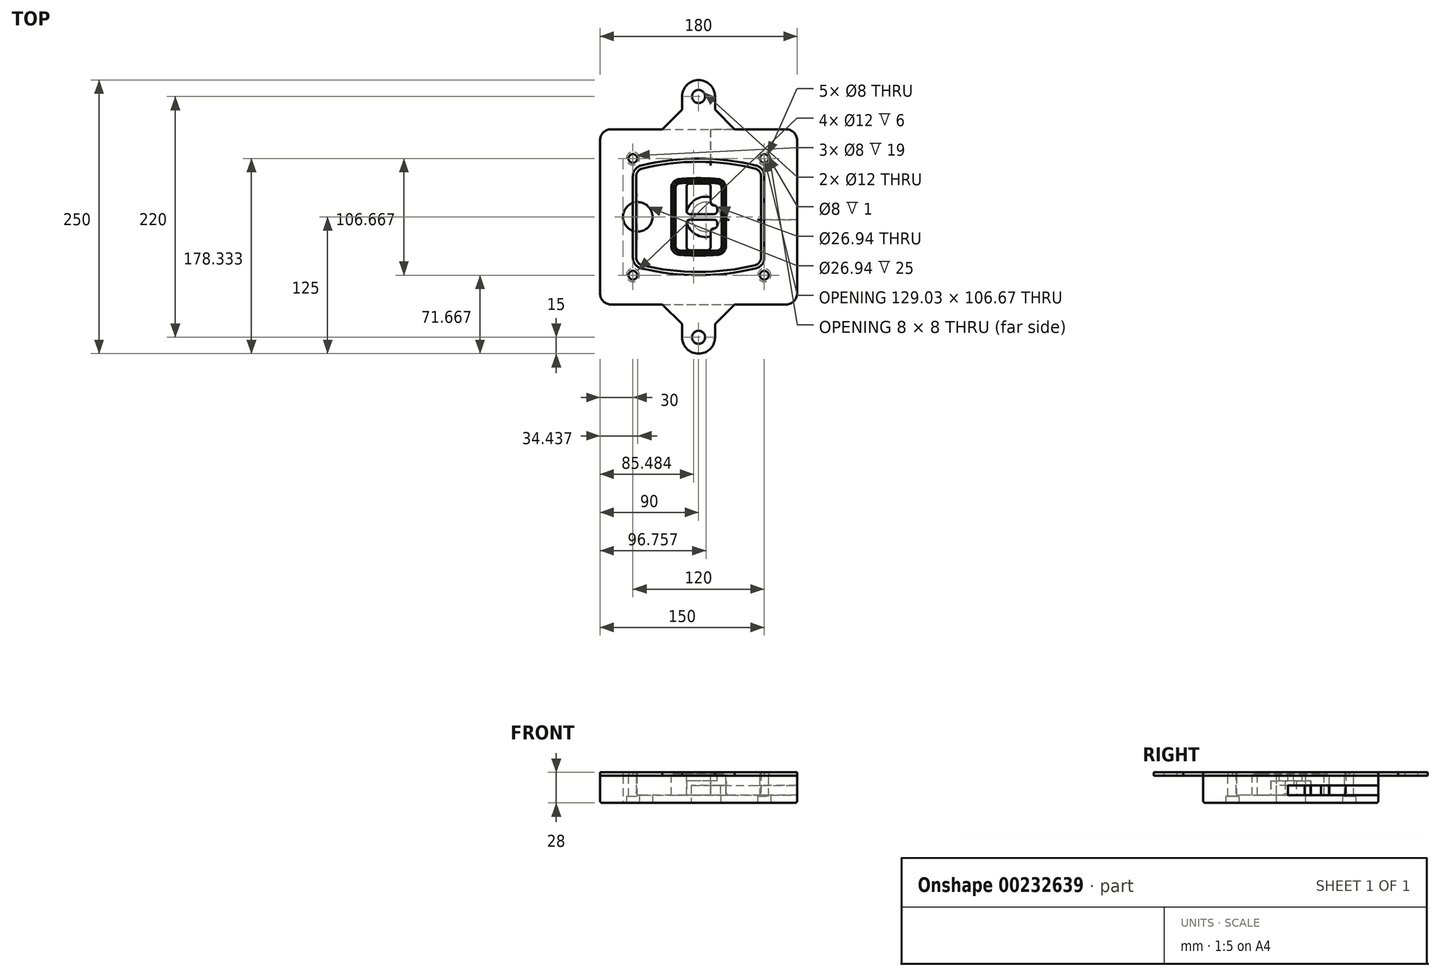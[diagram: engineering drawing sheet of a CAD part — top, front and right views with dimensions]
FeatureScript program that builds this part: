
annotation { "Feature Type Name" : "Feature", "Feature Type Description" : "" }
export const myFeature = defineFeature(function(context is Context, id is Id, definition is map)
    precondition{}
    {
        {
            var Q0;
            Q0=qCreatedBy(makeId("Top.planeOp"),FACE);
            var sketch = newSketch(context, id + "F0", { "sketchPlane" : qUnion([Q0])});
            skPoint(sketch, "E0.rect.middle", {"position": v(0, 0) * mm});
            skLineSegment(sketch, "E1.bottom", {"start": v(-80, -80) * mm, "end": v(80, -80) * mm});
            skLineSegment(sketch, "E1.top", {"start": v(-80, 80) * mm, "end": v(80, 80) * mm});
            skLineSegment(sketch, "E1.left", {"start": v(-90, -70) * mm, "end": v(-90, 70) * mm});
            skLineSegment(sketch, "E1.right", {"start": v(90, -70) * mm, "end": v(90, 70) * mm});
            skLineSegment(sketch, "E2", {"start": v(-90, 80) * mm, "end": v(90, -80) * mm, "construction": true});
            skLineSegment(sketch, "E3", {"start": v(90, 80) * mm, "end": v(-90, -80) * mm, "construction": true});
            skCircle(sketch, "E4", {"center": v(-60, 53.33) * mm, "radius": 4 * mm});
            skCircle(sketch, "E5", {"center": v(60, 53.33) * mm, "radius": 4 * mm});
            skCircle(sketch, "E6", {"center": v(60, -53.33) * mm, "radius": 4 * mm});
            skCircle(sketch, "E7", {"center": v(-60, -53.33) * mm, "radius": 4 * mm});
            skLineSegment(sketch, "E8", {"start": v(-60, 53.33) * mm, "end": v(60, 53.33) * mm, "construction": true});
            skLineSegment(sketch, "E9", {"start": v(60, 53.33) * mm, "end": v(60, -53.33) * mm, "construction": true});
            skLineSegment(sketch, "E10", {"start": v(60, -53.33) * mm, "end": v(-60, -53.33) * mm, "construction": true});
            skLineSegment(sketch, "E11", {"start": v(-60, -53.33) * mm, "end": v(-60, 53.33) * mm, "construction": true});
            skLineSegment(sketch, "E12", {"start": v(-60, 37.3) * mm, "end": v(-60, -37.3) * mm});
            skLineSegment(sketch, "E13", {"start": v(60, 37.3) * mm, "end": v(60, -37.3) * mm});
            skArc(sketch, "E14", {"start": v(52.38, 47.01) * mm, "mid": v(0, 53.33) * mm, "end": v(-52.38, 47.01) * mm});
            skArc(sketch, "E15", {"start": v(-52.38, -47.01) * mm, "mid": v(0, -53.33) * mm, "end": v(52.38, -47.01) * mm});
            skLineSegment(sketch, "E16", {"start": v(-60, 0) * mm, "end": v(60, 0) * mm, "construction": true});
            skPoint(sketch, "E17.visualSharp", {"position": v(-60, -45) * mm});
            skArc(sketch, "E17.filletArc", {"start": v(-60, -37.3) * mm, "mid": v(-57.87, -43.47) * mm, "end": v(-52.38, -47.01) * mm});
            skPoint(sketch, "E18.visualSharp", {"position": v(-60, 45) * mm});
            skArc(sketch, "E18.filletArc", {"start": v(-52.38, 47.01) * mm, "mid": v(-57.87, 43.47) * mm, "end": v(-60, 37.3) * mm});
            skPoint(sketch, "E19.visualSharp", {"position": v(60, 45) * mm});
            skArc(sketch, "E19.filletArc", {"start": v(60, 37.3) * mm, "mid": v(57.87, 43.47) * mm, "end": v(52.38, 47.01) * mm});
            skPoint(sketch, "E20.visualSharp", {"position": v(60, -45) * mm});
            skArc(sketch, "E20.filletArc", {"start": v(52.38, -47.01) * mm, "mid": v(57.87, -43.47) * mm, "end": v(60, -37.3) * mm});
            skPoint(sketch, "E21.visualSharp", {"position": v(-90, 80) * mm});
            skArc(sketch, "E21.filletArc", {"start": v(-80, 80) * mm, "mid": v(-87.07, 77.07) * mm, "end": v(-90, 70) * mm});
            skPoint(sketch, "E22.visualSharp", {"position": v(90, 80) * mm});
            skArc(sketch, "E22.filletArc", {"start": v(90, 70) * mm, "mid": v(87.07, 77.07) * mm, "end": v(80, 80) * mm});
            skPoint(sketch, "E23.visualSharp", {"position": v(90, -80) * mm});
            skArc(sketch, "E23.filletArc", {"start": v(80, -80) * mm, "mid": v(87.07, -77.07) * mm, "end": v(90, -70) * mm});
            skPoint(sketch, "E24.visualSharp", {"position": v(-90, -80) * mm});
            skArc(sketch, "E24.filletArc", {"start": v(-90, -70) * mm, "mid": v(-87.07, -77.07) * mm, "end": v(-80, -80) * mm});
            skArc(sketch, "E25.0", {"start": v(57, 37.3) * mm, "mid": v(55.5, 41.62) * mm, "end": v(51.67, 44.1) * mm});
            skLineSegment(sketch, "E25.1", {"start": v(57, 37.3) * mm, "end": v(57, -37.3) * mm});
            skArc(sketch, "E25.2", {"start": v(51.67, -44.1) * mm, "mid": v(55.5, -41.62) * mm, "end": v(57, -37.3) * mm});
            skArc(sketch, "E25.3", {"start": v(-51.67, -44.1) * mm, "mid": v(0, -50.33) * mm, "end": v(51.67, -44.1) * mm});
            skArc(sketch, "E25.4", {"start": v(-57, -37.3) * mm, "mid": v(-55.5, -41.62) * mm, "end": v(-51.67, -44.1) * mm});
            skArc(sketch, "E25.5", {"start": v(51.67, 44.1) * mm, "mid": v(0, 50.33) * mm, "end": v(-51.67, 44.1) * mm});
            skLineSegment(sketch, "E25.6", {"start": v(-57, 37.3) * mm, "end": v(-57, -37.3) * mm});
            skArc(sketch, "E25.7", {"start": v(-51.67, 44.1) * mm, "mid": v(-55.5, 41.62) * mm, "end": v(-57, 37.3) * mm});
            skArc(sketch, "E26.0", {"start": v(-53.33, 50.9) * mm, "mid": v(-61.01, 45.94) * mm, "end": v(-64, 37.3) * mm});
            skArc(sketch, "E26.1", {"start": v(53.33, 50.9) * mm, "mid": v(0, 57.33) * mm, "end": v(-53.33, 50.9) * mm});
            skArc(sketch, "E26.2", {"start": v(64, 37.3) * mm, "mid": v(61.01, 45.94) * mm, "end": v(53.33, 50.9) * mm});
            skLineSegment(sketch, "E26.3", {"start": v(64, 37.3) * mm, "end": v(64, -37.3) * mm});
            skArc(sketch, "E26.4", {"start": v(53.33, -50.9) * mm, "mid": v(61.01, -45.94) * mm, "end": v(64, -37.3) * mm});
            skLineSegment(sketch, "E26.5", {"start": v(-64, 37.3) * mm, "end": v(-64, -37.3) * mm});
            skArc(sketch, "E26.6", {"start": v(-53.33, -50.9) * mm, "mid": v(0, -57.33) * mm, "end": v(53.33, -50.9) * mm});
            skArc(sketch, "E26.7", {"start": v(-64, -37.3) * mm, "mid": v(-61.01, -45.94) * mm, "end": v(-53.33, -50.9) * mm});
            skSolve(sketch);
        }
        {
            var Q0;
            Q0=makeQuery(id+"F0.imprint","IMPRINT",FACE,{"disambiguationData":[TD([[makeQuery(id+"F0.imprint","IMPRINT",EDGE,{"derivedFrom":sQuery(id+"F0.wireOp",EDGE,"E1.bottom")}),1.0]])]});
            var Q1;
            Q1=makeQuery(id+"F0.imprint","IMPRINT",FACE,{"disambiguationData":[TD([[makeQuery(id+"F0.imprint","IMPRINT",EDGE,{"derivedFrom":sQuery(id+"F0.wireOp",EDGE,"E12")}),1.0]])]});
            var Q2;
            Q2=makeQuery(id+"F0.imprint","IMPRINT",FACE,{"disambiguationData":[TD([[makeQuery(id+"F0.imprint","IMPRINT",EDGE,{"derivedFrom":sQuery(id+"F0.wireOp",EDGE,"E25.0")}),1.0]])]});
            var Q3;
            Q3=makeQuery(id+"F0.imprint","IMPRINT",FACE,{"disambiguationData":[TD([[makeQuery(id+"F0.imprint","IMPRINT",EDGE,{"derivedFrom":sQuery(id+"F0.wireOp",EDGE,"E12")}),-1.0]])]});
            extrude(context, id + "F1", {"entities" : qUnion([Q0, Q1, Q2, Q3]), "oppositeDirection" : true, "depth" : 25 * mm});
        }
        {
            var Q0;
            Q0=makeQuery(id+"F0.imprint","IMPRINT",FACE,{"disambiguationData":[TD([[makeQuery(id+"F0.imprint","IMPRINT",EDGE,{"derivedFrom":sQuery(id+"F0.wireOp",EDGE,"E12")}),1.0]])]});
            extrude(context, id + "F2", {"entities" : qUnion([Q0]), "operationType" : NewBodyOperationType.ADD, "depth" : 3 * mm});
        }
        {
            var Q0;
            Q0=makeQuery(id+"F0.imprint","IMPRINT",FACE,{"disambiguationData":[TD([[makeQuery(id+"F0.imprint","IMPRINT",EDGE,{"derivedFrom":sQuery(id+"F0.wireOp",EDGE,"E25.0")}),1.0]])]});
            extrude(context, id + "F3", {"entities" : qUnion([Q0]), "operationType" : NewBodyOperationType.REMOVE, "oppositeDirection" : true, "depth" : 18 * mm});
        }
        {
            var Q0;
            Q0=makeQuery(id+"F2.opExtrude","CAP_FACE",FACE,{"disambiguationData":[OSD([sQuery(id+"F0.wireOp",EDGE,"E12"),sQuery(id+"F0.wireOp",EDGE,"E13"),sQuery(id+"F0.wireOp",EDGE,"E14"),sQuery(id+"F0.wireOp",EDGE,"E15"),sQuery(id+"F0.wireOp",EDGE,"E17.filletArc"),sQuery(id+"F0.wireOp",EDGE,"E18.filletArc"),sQuery(id+"F0.wireOp",EDGE,"E19.filletArc"),sQuery(id+"F0.wireOp",EDGE,"E20.filletArc"),sQuery(id+"F0.wireOp",EDGE,"E25.0"),sQuery(id+"F0.wireOp",EDGE,"E25.1"),sQuery(id+"F0.wireOp",EDGE,"E25.2"),sQuery(id+"F0.wireOp",EDGE,"E25.3"),sQuery(id+"F0.wireOp",EDGE,"E25.4"),sQuery(id+"F0.wireOp",EDGE,"E25.5"),sQuery(id+"F0.wireOp",EDGE,"E25.6"),sQuery(id+"F0.wireOp",EDGE,"E25.7")])],"isStart":false});
            var sketch = newSketch(context, id + "F4", { "sketchPlane" : qUnion([Q0])});
            skArc(sketch, "E27.0", {"start": v(-17.7, -34.56) * mm, "mid": v(0, -35.33) * mm, "end": v(17.7, -34.56) * mm});
            skArc(sketch, "E28.0", {"start": v(17.7, 34.56) * mm, "mid": v(0, 35.33) * mm, "end": v(-17.7, 34.56) * mm});
            skLineSegment(sketch, "E29", {"start": v(-25, 26.59) * mm, "end": v(-25, -26.59) * mm});
            skLineSegment(sketch, "E30", {"start": v(25, 26.59) * mm, "end": v(25, -26.59) * mm});
            skLineSegment(sketch, "E31", {"start": v(-25, 33.78) * mm, "end": v(25, 33.78) * mm, "construction": true});
            skLineSegment(sketch, "E32", {"start": v(-25, -33.78) * mm, "end": v(25, -33.78) * mm, "construction": true});
            skPoint(sketch, "E33.visualSharp", {"position": v(-25, 33.78) * mm});
            skArc(sketch, "E33.filletArc", {"start": v(-17.7, 34.56) * mm, "mid": v(-22.9, 32) * mm, "end": v(-25, 26.59) * mm});
            skPoint(sketch, "E34.visualSharp", {"position": v(25, 33.78) * mm});
            skArc(sketch, "E34.filletArc", {"start": v(25, 26.59) * mm, "mid": v(22.9, 32) * mm, "end": v(17.7, 34.56) * mm});
            skPoint(sketch, "E35.visualSharp", {"position": v(25, -33.78) * mm});
            skArc(sketch, "E35.filletArc", {"start": v(17.7, -34.56) * mm, "mid": v(22.9, -32) * mm, "end": v(25, -26.59) * mm});
            skPoint(sketch, "E36.visualSharp", {"position": v(-25, -33.78) * mm});
            skArc(sketch, "E36.filletArc", {"start": v(-25, -26.59) * mm, "mid": v(-22.9, -32) * mm, "end": v(-17.7, -34.56) * mm});
            skArc(sketch, "E37.0", {"start": v(51.67, 44.1) * mm, "mid": v(0, 50.33) * mm, "end": v(-51.67, 44.1) * mm});
            skArc(sketch, "E37.1", {"start": v(-51.67, 44.1) * mm, "mid": v(-55.5, 41.62) * mm, "end": v(-57, 37.3) * mm});
            skLineSegment(sketch, "E37.2", {"start": v(-57, 37.3) * mm, "end": v(-57, -37.3) * mm});
            skArc(sketch, "E37.3", {"start": v(-57, -37.3) * mm, "mid": v(-55.5, -41.62) * mm, "end": v(-51.67, -44.1) * mm});
            skArc(sketch, "E37.4", {"start": v(-51.67, -44.1) * mm, "mid": v(0, -50.33) * mm, "end": v(51.67, -44.1) * mm});
            skArc(sketch, "E37.5", {"start": v(51.67, -44.1) * mm, "mid": v(55.5, -41.62) * mm, "end": v(57, -37.3) * mm});
            skLineSegment(sketch, "E37.6", {"start": v(57, 37.3) * mm, "end": v(57, -37.3) * mm});
            skArc(sketch, "E37.7", {"start": v(57, 37.3) * mm, "mid": v(55.5, 41.62) * mm, "end": v(51.67, 44.1) * mm});
            skLineSegment(sketch, "E38.0", {"start": v(23, 26.59) * mm, "end": v(23, -26.59) * mm});
            skArc(sketch, "E38.1", {"start": v(17.53, -32.56) * mm, "mid": v(21.42, -30.64) * mm, "end": v(23, -26.59) * mm});
            skArc(sketch, "E38.2", {"start": v(-17.53, -32.56) * mm, "mid": v(0, -33.33) * mm, "end": v(17.53, -32.56) * mm});
            skArc(sketch, "E38.3", {"start": v(-23, -26.59) * mm, "mid": v(-21.42, -30.64) * mm, "end": v(-17.53, -32.56) * mm});
            skLineSegment(sketch, "E38.4", {"start": v(-23, 26.59) * mm, "end": v(-23, -26.59) * mm});
            skArc(sketch, "E38.5", {"start": v(23, 26.59) * mm, "mid": v(21.42, 30.64) * mm, "end": v(17.53, 32.56) * mm});
            skArc(sketch, "E38.6", {"start": v(-17.53, 32.56) * mm, "mid": v(-21.42, 30.64) * mm, "end": v(-23, 26.59) * mm});
            skArc(sketch, "E38.7", {"start": v(17.53, 32.56) * mm, "mid": v(0, 33.33) * mm, "end": v(-17.53, 32.56) * mm});
            skArc(sketch, "E39.0", {"start": v(21, 26.59) * mm, "mid": v(19.95, 29.29) * mm, "end": v(17.35, 30.57) * mm});
            skLineSegment(sketch, "E39.1", {"start": v(21, 26.59) * mm, "end": v(21, -26.59) * mm});
            skArc(sketch, "E39.2", {"start": v(17.35, -30.57) * mm, "mid": v(19.95, -29.29) * mm, "end": v(21, -26.59) * mm});
            skArc(sketch, "E39.3", {"start": v(-17.35, -30.57) * mm, "mid": v(0, -31.33) * mm, "end": v(17.35, -30.57) * mm});
            skArc(sketch, "E39.4", {"start": v(-21, -26.59) * mm, "mid": v(-19.95, -29.29) * mm, "end": v(-17.35, -30.57) * mm});
            skArc(sketch, "E39.5", {"start": v(17.35, 30.57) * mm, "mid": v(0, 31.33) * mm, "end": v(-17.35, 30.57) * mm});
            skLineSegment(sketch, "E39.6", {"start": v(-21, 26.59) * mm, "end": v(-21, -26.59) * mm});
            skArc(sketch, "E39.7", {"start": v(-17.35, 30.57) * mm, "mid": v(-19.95, 29.29) * mm, "end": v(-21, 26.59) * mm});
            skLineSegment(sketch, "E40", {"start": v(-25, 0) * mm, "end": v(25, 0) * mm, "construction": true});
            skLineSegment(sketch, "E41", {"start": v(-11, 5.5) * mm, "end": v(-11, 27.5) * mm});
            skLineSegment(sketch, "E42", {"start": v(-8, 30.5) * mm, "end": v(8, 30.5) * mm});
            skLineSegment(sketch, "E43", {"start": v(11, 27.5) * mm, "end": v(11, 13.5) * mm});
            skLineSegment(sketch, "E44", {"start": v(14, 10.5) * mm, "end": v(14, 10.5) * mm});
            skLineSegment(sketch, "E45", {"start": v(17, 7.5) * mm, "end": v(17, 5.5) * mm});
            skLineSegment(sketch, "E46", {"start": v(14, 2.5) * mm, "end": v(-8, 2.5) * mm});
            skPoint(sketch, "E47.visualSharp", {"position": v(-11, 30.5) * mm});
            skArc(sketch, "E47.filletArc", {"start": v(-8, 30.5) * mm, "mid": v(-10.12, 29.62) * mm, "end": v(-11, 27.5) * mm});
            skPoint(sketch, "E48.visualSharp", {"position": v(11, 30.5) * mm});
            skArc(sketch, "E48.filletArc", {"start": v(11, 27.5) * mm, "mid": v(10.12, 29.62) * mm, "end": v(8, 30.5) * mm});
            skPoint(sketch, "E49.visualSharp", {"position": v(11, 10.5) * mm});
            skArc(sketch, "E49.filletArc", {"start": v(11, 13.5) * mm, "mid": v(11.88, 11.38) * mm, "end": v(14, 10.5) * mm});
            skPoint(sketch, "E50.visualSharp", {"position": v(17, 10.5) * mm});
            skArc(sketch, "E50.filletArc", {"start": v(17, 7.5) * mm, "mid": v(16.12, 9.62) * mm, "end": v(14, 10.5) * mm});
            skPoint(sketch, "E51.visualSharp", {"position": v(17, 2.5) * mm});
            skArc(sketch, "E51.filletArc", {"start": v(14, 2.5) * mm, "mid": v(16.12, 3.38) * mm, "end": v(17, 5.5) * mm});
            skPoint(sketch, "E52.visualSharp", {"position": v(-11, 2.5) * mm});
            skArc(sketch, "E52.filletArc", {"start": v(-11, 5.5) * mm, "mid": v(-10.12, 3.38) * mm, "end": v(-8, 2.5) * mm});
            skLineSegment(sketch, "E53.0.MirrorCS", {"start": v(14, -2.5) * mm, "end": v(-8, -2.5) * mm});
            skArc(sketch, "E54.0.MirrorCS", {"start": v(-11, -5.5) * mm, "mid": v(-10.12, -3.38) * mm, "end": v(-8, -2.5) * mm});
            skLineSegment(sketch, "E55.0.MirrorCS", {"start": v(-11, -5.5) * mm, "end": v(-11, -27.5) * mm});
            skArc(sketch, "E56.0.MirrorCS", {"start": v(-8, -30.5) * mm, "mid": v(-10.12, -29.62) * mm, "end": v(-11, -27.5) * mm});
            skLineSegment(sketch, "E57.0.MirrorCS", {"start": v(-8, -30.5) * mm, "end": v(8, -30.5) * mm});
            skArc(sketch, "E58.0.MirrorCS", {"start": v(11, -27.5) * mm, "mid": v(10.12, -29.62) * mm, "end": v(8, -30.5) * mm});
            skLineSegment(sketch, "E59.0.MirrorCS", {"start": v(11, -27.5) * mm, "end": v(11, -13.5) * mm});
            skArc(sketch, "E60.0.MirrorCS", {"start": v(11, -13.5) * mm, "mid": v(11.88, -11.38) * mm, "end": v(14, -10.5) * mm});
            skArc(sketch, "E61.0.MirrorCS", {"start": v(17, -7.5) * mm, "mid": v(16.12, -9.62) * mm, "end": v(14, -10.5) * mm});
            skLineSegment(sketch, "E62.0.MirrorCS", {"start": v(17, -7.5) * mm, "end": v(17, -5.5) * mm});
            skArc(sketch, "E63.0.MirrorCS", {"start": v(14, -2.5) * mm, "mid": v(16.12, -3.38) * mm, "end": v(17, -5.5) * mm});
            skSolve(sketch);
        }
        {
            var Q0;
            Q0=makeQuery(id+"F4.imprint","IMPRINT",FACE,{"disambiguationData":[TD([[makeQuery(id+"F4.imprint","IMPRINT",EDGE,{"derivedFrom":sQuery(id+"F4.wireOp",EDGE,"E27.0")}),1.0]])]});
            var Q1;
            Q1=makeQuery(id+"F4.imprint","IMPRINT",FACE,{"disambiguationData":[TD([[makeQuery(id+"F4.imprint","IMPRINT",EDGE,{"derivedFrom":sQuery(id+"F4.wireOp",EDGE,"E38.0")}),-1.0]])]});
            var Q2;
            Q2=makeQuery(id+"F4.imprint","IMPRINT",FACE,{"disambiguationData":[TD([[makeQuery(id+"F4.imprint","IMPRINT",EDGE,{"derivedFrom":sQuery(id+"F4.wireOp",EDGE,"E39.0")}),1.0]])]});
            extrude(context, id + "F5", {"entities" : qUnion([Q0, Q1, Q2]), "operationType" : NewBodyOperationType.ADD, "endBound" : BoundingType.UP_TO_NEXT, "oppositeDirection" : true, "depth" : 25 * mm});
        }
        {
            var Q0;
            Q0=makeQuery(id+"F4.imprint","IMPRINT",FACE,{"disambiguationData":[TD([[makeQuery(id+"F4.imprint","IMPRINT",EDGE,{"derivedFrom":sQuery(id+"F4.wireOp",EDGE,"E38.0")}),-1.0]])]});
            extrude(context, id + "F6", {"entities" : qUnion([Q0]), "operationType" : NewBodyOperationType.REMOVE, "oppositeDirection" : true, "depth" : 2 * mm});
        }
        {
            var Q0;
            Q0=makeQuery(id+"F1.opExtrude","CAP_FACE",FACE,{"disambiguationData":[OSD([sQuery(id+"F0.wireOp",EDGE,"E1.bottom"),sQuery(id+"F0.wireOp",EDGE,"E1.top"),sQuery(id+"F0.wireOp",EDGE,"E1.left"),sQuery(id+"F0.wireOp",EDGE,"E1.right"),sQuery(id+"F0.wireOp",EDGE,"E4"),sQuery(id+"F0.wireOp",EDGE,"E5"),sQuery(id+"F0.wireOp",EDGE,"E6"),sQuery(id+"F0.wireOp",EDGE,"E7"),sQuery(id+"F0.wireOp",EDGE,"E21.filletArc"),sQuery(id+"F0.wireOp",EDGE,"E22.filletArc"),sQuery(id+"F0.wireOp",EDGE,"E23.filletArc"),sQuery(id+"F0.wireOp",EDGE,"E24.filletArc")])],"isStart":false});
            var sketch = newSketch(context, id + "F7", { "sketchPlane" : qUnion([Q0])});
            skCircle(sketch, "E64", {"center": v(6.76, 0) * mm, "radius": 13.47 * mm});
            skCircle(sketch, "E65", {"center": v(-55.56, 0) * mm, "radius": 13.47 * mm});
            skLineSegment(sketch, "E66", {"start": v(90, 0) * mm, "end": v(-90, 0) * mm});
            skCircle(sketch, "E67", {"center": v(6.76, 0) * mm, "radius": 18.47 * mm});
            skCircle(sketch, "E68", {"center": v(60, -53.33) * mm, "radius": 6 * mm});
            skCircle(sketch, "E69", {"center": v(-60, -53.33) * mm, "radius": 6 * mm});
            skCircle(sketch, "E70", {"center": v(-60, 53.33) * mm, "radius": 6 * mm});
            skCircle(sketch, "E71", {"center": v(60, 53.33) * mm, "radius": 6 * mm});
            skSolve(sketch);
        }
        {
            var Q0;
            {var subQ1=sQuery(id+"F7.wireOp",EDGE,"E66");var subQ4=sQuery(id+"F7.wireOp",EDGE,"E64");var subQ6=makeQuery(id+"F7.imprint","INTERSECT",VERTEX,{"disambiguationData":[OD(0.0)],"derivedFrom":[subQ4,subQ1]});Q0=makeQuery(id+"F7.imprint","IMPRINT",FACE,{"disambiguationData":[TD([[makeQuery(id+"F7.imprint","IMPRINT",EDGE,{"disambiguationData":[TD([[subQ6,-1.0]])],"derivedFrom":subQ4}),-1.0]])]});}
            var Q1;
            {var subQ0=sQuery(id+"F7.wireOp",EDGE,"E66");var subQ1=sQuery(id+"F7.wireOp",EDGE,"E64");var subQ3=makeQuery(id+"F7.imprint","INTERSECT",VERTEX,{"disambiguationData":[OD(0.0)],"derivedFrom":[subQ1,subQ0]});Q1=makeQuery(id+"F7.imprint","IMPRINT",FACE,{"disambiguationData":[TD([[makeQuery(id+"F7.imprint","IMPRINT",EDGE,{"disambiguationData":[TD([[subQ3,-1.0]])],"derivedFrom":subQ1}),1.0]])]});}
            var Q2;
            {var subQ0=sQuery(id+"F7.wireOp",EDGE,"E66");var subQ1=sQuery(id+"F7.wireOp",EDGE,"E64");var subQ3=makeQuery(id+"F7.imprint","INTERSECT",VERTEX,{"disambiguationData":[OD(0.0)],"derivedFrom":[subQ1,subQ0]});Q2=makeQuery(id+"F7.imprint","IMPRINT",FACE,{"disambiguationData":[TD([[makeQuery(id+"F7.imprint","IMPRINT",EDGE,{"disambiguationData":[TD([[subQ3,1.0]])],"derivedFrom":subQ1}),1.0]])]});}
            var Q3;
            {var subQ1=sQuery(id+"F7.wireOp",EDGE,"E66");var subQ4=sQuery(id+"F7.wireOp",EDGE,"E64");var subQ6=makeQuery(id+"F7.imprint","INTERSECT",VERTEX,{"disambiguationData":[OD(0.0)],"derivedFrom":[subQ4,subQ1]});Q3=makeQuery(id+"F7.imprint","IMPRINT",FACE,{"disambiguationData":[TD([[makeQuery(id+"F7.imprint","IMPRINT",EDGE,{"disambiguationData":[TD([[subQ6,1.0]])],"derivedFrom":subQ4}),-1.0]])]});}
            extrude(context, id + "F8", {"entities" : qUnion([Q0, Q1, Q2, Q3]), "operationType" : NewBodyOperationType.ADD, "oppositeDirection" : true, "depth" : 20 * mm});
        }
        {
            var Q0;
            {var subQ0=sQuery(id+"F7.wireOp",EDGE,"E66");var subQ1=sQuery(id+"F7.wireOp",EDGE,"E64");var subQ3=makeQuery(id+"F7.imprint","INTERSECT",VERTEX,{"disambiguationData":[OD(0.0)],"derivedFrom":[subQ1,subQ0]});Q0=makeQuery(id+"F7.imprint","IMPRINT",FACE,{"disambiguationData":[TD([[makeQuery(id+"F7.imprint","IMPRINT",EDGE,{"disambiguationData":[TD([[subQ3,-1.0]])],"derivedFrom":subQ1}),1.0]])]});}
            var Q1;
            {var subQ0=sQuery(id+"F7.wireOp",EDGE,"E66");var subQ1=sQuery(id+"F7.wireOp",EDGE,"E64");var subQ3=makeQuery(id+"F7.imprint","INTERSECT",VERTEX,{"disambiguationData":[OD(0.0)],"derivedFrom":[subQ1,subQ0]});Q1=makeQuery(id+"F7.imprint","IMPRINT",FACE,{"disambiguationData":[TD([[makeQuery(id+"F7.imprint","IMPRINT",EDGE,{"disambiguationData":[TD([[subQ3,1.0]])],"derivedFrom":subQ1}),1.0]])]});}
            extrude(context, id + "F9", {"entities" : qUnion([Q0, Q1]), "operationType" : NewBodyOperationType.REMOVE, "oppositeDirection" : true, "depth" : 16 * mm});
        }
        {
            var Q0;
            {var subQ0=sQuery(id+"F7.wireOp",EDGE,"E66");var subQ1=sQuery(id+"F7.wireOp",EDGE,"E65");var subQ3=makeQuery(id+"F7.imprint","INTERSECT",VERTEX,{"disambiguationData":[OD(0.0)],"derivedFrom":[subQ1,subQ0]});Q0=makeQuery(id+"F7.imprint","IMPRINT",FACE,{"disambiguationData":[TD([[makeQuery(id+"F7.imprint","IMPRINT",EDGE,{"disambiguationData":[TD([[subQ3,-1.0]])],"derivedFrom":subQ1}),1.0]])]});}
            var Q1;
            {var subQ0=sQuery(id+"F7.wireOp",EDGE,"E66");var subQ1=sQuery(id+"F7.wireOp",EDGE,"E65");var subQ3=makeQuery(id+"F7.imprint","INTERSECT",VERTEX,{"disambiguationData":[OD(0.0)],"derivedFrom":[subQ1,subQ0]});Q1=makeQuery(id+"F7.imprint","IMPRINT",FACE,{"disambiguationData":[TD([[makeQuery(id+"F7.imprint","IMPRINT",EDGE,{"disambiguationData":[TD([[subQ3,1.0]])],"derivedFrom":subQ1}),1.0]])]});}
            extrude(context, id + "F10", {"entities" : qUnion([Q0, Q1]), "operationType" : NewBodyOperationType.REMOVE, "oppositeDirection" : true, "depth" : 25 * mm});
        }
        {
            var Q0;
            Q0=makeQuery(id+"F7.imprint","IMPRINT",FACE,{"disambiguationData":[TD([[makeQuery(id+"F7.imprint","IMPRINT",EDGE,{"derivedFrom":sQuery(id+"F7.wireOp",EDGE,"E68")}),1.0]])]});
            var Q1;
            Q1=makeQuery(id+"F7.imprint","IMPRINT",FACE,{"disambiguationData":[TD([[makeQuery(id+"F7.imprint","IMPRINT",EDGE,{"derivedFrom":makeQuery(id+"F1.opExtrude","CAP_EDGE",EDGE,{"disambiguationData":[OSD([sQuery(id+"F0.wireOp",EDGE,"E5")])],"isStart":false})}),-1.0]])]});
            var Q2;
            Q2=makeQuery(id+"F7.imprint","IMPRINT",FACE,{"disambiguationData":[TD([[makeQuery(id+"F7.imprint","IMPRINT",EDGE,{"derivedFrom":sQuery(id+"F7.wireOp",EDGE,"E69")}),1.0]])]});
            var Q3;
            Q3=makeQuery(id+"F7.imprint","IMPRINT",FACE,{"disambiguationData":[TD([[makeQuery(id+"F7.imprint","IMPRINT",EDGE,{"derivedFrom":makeQuery(id+"F1.opExtrude","CAP_EDGE",EDGE,{"disambiguationData":[OSD([sQuery(id+"F0.wireOp",EDGE,"E4")])],"isStart":false})}),-1.0]])]});
            var Q4;
            Q4=makeQuery(id+"F7.imprint","IMPRINT",FACE,{"disambiguationData":[TD([[makeQuery(id+"F7.imprint","IMPRINT",EDGE,{"derivedFrom":sQuery(id+"F7.wireOp",EDGE,"E70")}),1.0]])]});
            var Q5;
            Q5=makeQuery(id+"F7.imprint","IMPRINT",FACE,{"disambiguationData":[TD([[makeQuery(id+"F7.imprint","IMPRINT",EDGE,{"derivedFrom":makeQuery(id+"F1.opExtrude","CAP_EDGE",EDGE,{"disambiguationData":[OSD([sQuery(id+"F0.wireOp",EDGE,"E7")])],"isStart":false})}),-1.0]])]});
            var Q6;
            Q6=makeQuery(id+"F7.imprint","IMPRINT",FACE,{"disambiguationData":[TD([[makeQuery(id+"F7.imprint","IMPRINT",EDGE,{"derivedFrom":sQuery(id+"F7.wireOp",EDGE,"E71")}),1.0]])]});
            var Q7;
            Q7=makeQuery(id+"F7.imprint","IMPRINT",FACE,{"disambiguationData":[TD([[makeQuery(id+"F7.imprint","IMPRINT",EDGE,{"derivedFrom":makeQuery(id+"F1.opExtrude","CAP_EDGE",EDGE,{"disambiguationData":[OSD([sQuery(id+"F0.wireOp",EDGE,"E6")])],"isStart":false})}),-1.0]])]});
            extrude(context, id + "F11", {"entities" : qUnion([Q0, Q1, Q2, Q3, Q4, Q5, Q6, Q7]), "operationType" : NewBodyOperationType.REMOVE, "oppositeDirection" : true, "depth" : 6 * mm});
        }
        {
            var Q0;
            Q0=makeQuery(id+"F9.boolean.opBoolean","COPY",FACE,{"derivedFrom":makeQuery(id+"F9.opExtrude","CAP_FACE",FACE,{"disambiguationData":[OSD([sQuery(id+"F7.wireOp",EDGE,"E64")])],"isStart":false})});
            var sketch = newSketch(context, id + "F12", { "sketchPlane" : qUnion([Q0])});
            skArc(sketch, "E72.0", {"start": v(11, -88.19) * mm, "mid": v(97.1, -83.6) * mm, "end": v(92.5, 2.5) * mm});
            skLineSegment(sketch, "E72.1", {"start": v(11, -17.97) * mm, "end": v(11, -17.97) * mm});
            skLineSegment(sketch, "E73", {"start": v(92.5, -105.13) * mm, "end": v(102.3, -105.13) * mm});
            skLineSegment(sketch, "E74.0", {"start": v(92.5, 2.5) * mm, "end": v(14, 2.5) * mm});
            skArc(sketch, "E74.1", {"start": v(14, 2.5) * mm, "mid": v(16.12, 3.38) * mm, "end": v(17, 5.5) * mm});
            skLineSegment(sketch, "E74.2", {"start": v(17, 7.5) * mm, "end": v(17, 5.5) * mm});
            skArc(sketch, "E74.3", {"start": v(17, 7.5) * mm, "mid": v(16.12, 9.62) * mm, "end": v(14, 10.5) * mm});
            skArc(sketch, "E74.4", {"start": v(11, 13.5) * mm, "mid": v(11.88, 11.38) * mm, "end": v(14, 10.5) * mm});
            skLineSegment(sketch, "E74.5", {"start": v(11, 13.5) * mm, "end": v(11, -88.19) * mm});
            skLineSegment(sketch, "E74.7", {"start": v(92.5, -2.5) * mm, "end": v(14, -2.5) * mm});
            skArc(sketch, "E74.8", {"start": v(14, -2.5) * mm, "mid": v(16.12, -3.38) * mm, "end": v(17, -5.5) * mm});
            skLineSegment(sketch, "E74.9", {"start": v(17, -7.5) * mm, "end": v(17, -5.5) * mm});
            skArc(sketch, "E74.10", {"start": v(17, -7.5) * mm, "mid": v(16.12, -9.62) * mm, "end": v(14, -10.5) * mm});
            skArc(sketch, "E74.11", {"start": v(11, -13.5) * mm, "mid": v(11.88, -11.38) * mm, "end": v(14, -10.5) * mm});
            skLineSegment(sketch, "E74.12", {"start": v(11, -17.97) * mm, "end": v(11, -13.5) * mm});
            skPoint(sketch, "E75.orphan", {"position": v(11, -27.5) * mm});
            skPoint(sketch, "E76.orphan", {"position": v(-8, -2.5) * mm});
            skPoint(sketch, "E77.orphan", {"position": v(-8, 2.5) * mm});
            skPoint(sketch, "E78.orphan", {"position": v(11, 27.5) * mm});
            skSolve(sketch);
        }
        {
            var Q0;
            {var subQ7=sQuery(id+"F12.wireOp",EDGE,"E72.0");var subQ14=sQuery(id+"F12.wireOp",EDGE,"E72.1");var subQ16=sQuery(id+"F12.wireOp",EDGE,"E74.1");var subQ18=sQuery(id+"F12.wireOp",EDGE,"E74.8");Q0=qUnion([makeQuery(id+"F12.imprint","IMPRINT",FACE,{"disambiguationData":[TD([[makeQuery(id+"F12.imprint","IMPRINT",EDGE,{"derivedFrom":subQ7}),1.0]])]}),makeQuery(id+"F12.imprint","IMPRINT",FACE,{"disambiguationData":[TD([[makeQuery(id+"F12.imprint","IMPRINT",EDGE,{"derivedFrom":subQ14}),1.0]])]}),makeQuery(id+"F12.imprint","IMPRINT",FACE,{"disambiguationData":[TD([[makeQuery(id+"F12.imprint","IMPRINT",EDGE,{"derivedFrom":subQ16}),1.0]])]}),makeQuery(id+"F12.imprint","IMPRINT",FACE,{"disambiguationData":[TD([[makeQuery(id+"F12.imprint","IMPRINT",EDGE,{"derivedFrom":subQ18}),-1.0]])]})]);}
            var Q1;
            Q1=makeQuery(id+"F5.boolean.opBoolean","SPLIT",FACE,{"disambiguationData":[TD([makeQuery(id+"F5.opExtrude","SWEPT_FACE",FACE,{"disambiguationData":[OSD([sQuery(id+"F4.wireOp",EDGE,"E41")])]})])],"derivedFrom":makeQuery(id+"F3.boolean.opBoolean","COPY",FACE,{"derivedFrom":makeQuery(id+"F3.opExtrude","CAP_FACE",FACE,{"disambiguationData":[OSD([sQuery(id+"F0.wireOp",EDGE,"E25.0"),sQuery(id+"F0.wireOp",EDGE,"E25.1"),sQuery(id+"F0.wireOp",EDGE,"E25.2"),sQuery(id+"F0.wireOp",EDGE,"E25.3"),sQuery(id+"F0.wireOp",EDGE,"E25.4"),sQuery(id+"F0.wireOp",EDGE,"E25.5"),sQuery(id+"F0.wireOp",EDGE,"E25.6"),sQuery(id+"F0.wireOp",EDGE,"E25.7")])],"isStart":false})})});
            extrude(context, id + "F13", {"entities" : qUnion([Q0]), "operationType" : NewBodyOperationType.REMOVE, "endBound" : BoundingType.UP_TO_SURFACE, "endBoundEntityFace" : qUnion([Q1]), "depth" : 25 * mm});
        }
        {
            var Q0;
            Q0=makeQuery(id+"F3.boolean.opBoolean","COPY",EDGE,{"derivedFrom":makeQuery(id+"F3.opExtrude","CAP_EDGE",EDGE,{"disambiguationData":[OSD([sQuery(id+"F0.wireOp",EDGE,"E25.6")])],"isStart":false})});
            var Q1;
            Q1=makeQuery(id+"F8.boolean.opBoolean","INTERSECT",EDGE,{"derivedFrom":[makeQuery(id+"F5.opExtrude","SWEPT_FACE",FACE,{"disambiguationData":[OSD([sQuery(id+"F4.wireOp",EDGE,"E30")])]}),makeQuery(id+"F8.opExtrude","CAP_FACE",FACE,{"disambiguationData":[OSD([sQuery(id+"F7.wireOp",EDGE,"E67")])],"isStart":false})]});
            var Q2;
            Q2=makeQuery(id+"F8.boolean.opBoolean","INTERSECT",EDGE,{"disambiguationData":[OD(1.0)],"derivedFrom":[makeQuery(id+"F5.opExtrude","SWEPT_FACE",FACE,{"disambiguationData":[OSD([sQuery(id+"F4.wireOp",EDGE,"E30")])]}),makeQuery(id+"F8.opExtrude","SWEPT_FACE",FACE,{"disambiguationData":[OSD([sQuery(id+"F7.wireOp",EDGE,"E67")])]})]});
            var Q3;
            {var subQ0=makeQuery(id+"F3.boolean.opBoolean","COPY",FACE,{"derivedFrom":makeQuery(id+"F3.opExtrude","CAP_FACE",FACE,{"disambiguationData":[OSD([sQuery(id+"F0.wireOp",EDGE,"E25.0"),sQuery(id+"F0.wireOp",EDGE,"E25.1"),sQuery(id+"F0.wireOp",EDGE,"E25.2"),sQuery(id+"F0.wireOp",EDGE,"E25.3"),sQuery(id+"F0.wireOp",EDGE,"E25.4"),sQuery(id+"F0.wireOp",EDGE,"E25.5"),sQuery(id+"F0.wireOp",EDGE,"E25.6"),sQuery(id+"F0.wireOp",EDGE,"E25.7")])],"isStart":false})});var subQ1=sQuery(id+"F4.wireOp",EDGE,"E30");Q3=makeQuery(id+"F8.boolean.opBoolean","SPLIT",EDGE,{"disambiguationData":[TD([makeQuery(id+"F5.opExtrude","SWEPT_FACE",FACE,{"disambiguationData":[OSD([sQuery(id+"F4.wireOp",EDGE,"E35.filletArc")])]})])],"derivedFrom":makeQuery(id+"F5.opExtrude","TWEAK_EDGE",EDGE,{"derivedFrom":[subQ0,makeQuery(id+"F4.imprint","IMPRINT",EDGE,{"derivedFrom":subQ1})]})});}
            var Q4;
            {var subQ0=sQuery(id+"F0.wireOp",EDGE,"E25.0");var subQ1=sQuery(id+"F0.wireOp",EDGE,"E25.1");var subQ2=sQuery(id+"F0.wireOp",EDGE,"E25.2");var subQ3=sQuery(id+"F0.wireOp",EDGE,"E25.3");var subQ4=sQuery(id+"F0.wireOp",EDGE,"E25.4");var subQ5=sQuery(id+"F0.wireOp",EDGE,"E25.5");var subQ6=sQuery(id+"F0.wireOp",EDGE,"E25.6");var subQ7=sQuery(id+"F0.wireOp",EDGE,"E25.7");Q4=makeQuery(id+"F8.boolean.opBoolean","INTERSECT",EDGE,{"derivedFrom":[makeQuery(id+"F5.boolean.opBoolean","SPLIT",FACE,{"disambiguationData":[TD([makeQuery(id+"F2.opExtrude","SWEPT_FACE",FACE,{"disambiguationData":[OSD([subQ0])]})])],"derivedFrom":makeQuery(id+"F3.boolean.opBoolean","COPY",FACE,{"derivedFrom":makeQuery(id+"F3.opExtrude","CAP_FACE",FACE,{"disambiguationData":[OSD([subQ0,subQ1,subQ2,subQ3,subQ4,subQ5,subQ6,subQ7])],"isStart":false})})}),makeQuery(id+"F8.opExtrude","SWEPT_FACE",FACE,{"disambiguationData":[OSD([sQuery(id+"F7.wireOp",EDGE,"E67")])]})]});}
            var Q5;
            Q5=makeQuery(id+"F8.boolean.opBoolean","INTERSECT",EDGE,{"disambiguationData":[OD(0.0)],"derivedFrom":[makeQuery(id+"F5.opExtrude","SWEPT_FACE",FACE,{"disambiguationData":[OSD([sQuery(id+"F4.wireOp",EDGE,"E30")])]}),makeQuery(id+"F8.opExtrude","SWEPT_FACE",FACE,{"disambiguationData":[OSD([sQuery(id+"F7.wireOp",EDGE,"E67")])]})]});
            fillet(context, id + "F14", {"entities" : qUnion([Q0, Q1, Q2, Q3, Q4, Q5]), "radius" : 3 * mm, "tangentPropagation" : true, "allowEdgeOverflow" : false});
        }
        {
            var Q0;
            Q0=makeQuery(id+"F1.opExtrude","CAP_EDGE",EDGE,{"disambiguationData":[OSD([sQuery(id+"F0.wireOp",EDGE,"E1.bottom")])],"isStart":false});
            fillet(context, id + "F15", {"entities" : qUnion([Q0]), "radius" : 2 * mm, "tangentPropagation" : true, "allowEdgeOverflow" : false});
        }
        {
            var Q0;
            {var subQ0=sQuery(id+"F0.wireOp",EDGE,"E22.filletArc");var subQ1=sQuery(id+"F0.wireOp",EDGE,"E7");var subQ2=sQuery(id+"F0.wireOp",EDGE,"E6");var subQ3=sQuery(id+"F0.wireOp",EDGE,"E5");var subQ4=sQuery(id+"F0.wireOp",EDGE,"E4");var subQ5=sQuery(id+"F0.wireOp",EDGE,"E1.bottom");var subQ6=sQuery(id+"F0.wireOp",EDGE,"E21.filletArc");var subQ7=sQuery(id+"F0.wireOp",EDGE,"E1.top");var subQ8=sQuery(id+"F0.wireOp",EDGE,"E1.left");var subQ9=sQuery(id+"F0.wireOp",EDGE,"E1.right");var subQ10=sQuery(id+"F0.wireOp",EDGE,"E23.filletArc");var subQ11=sQuery(id+"F0.wireOp",EDGE,"E24.filletArc");Q0=makeQuery(id+"F2.boolean.opBoolean","SPLIT",FACE,{"disambiguationData":[TD([makeQuery(id+"F1.opExtrude","SWEPT_FACE",FACE,{"disambiguationData":[OSD([subQ5])]})])],"derivedFrom":makeQuery(id+"F1.opExtrude","CAP_FACE",FACE,{"disambiguationData":[OSD([subQ5,subQ7,subQ8,subQ9,subQ4,subQ3,subQ2,subQ1,subQ6,subQ0,subQ10,subQ11])],"isStart":true})});}
            var sketch = newSketch(context, id + "F16", { "sketchPlane" : qUnion([Q0])});
            skLineSegment(sketch, "E79", {"start": v(-33, 80) * mm, "end": v(-15, 98) * mm});
            skLineSegment(sketch, "E80", {"start": v(-15, 98) * mm, "end": v(-15, 110) * mm});
            skLineSegment(sketch, "E81", {"start": v(33, 80) * mm, "end": v(15, 98) * mm});
            skLineSegment(sketch, "E82", {"start": v(15, 98) * mm, "end": v(15, 110) * mm});
            skArc(sketch, "E83", {"start": v(15, 110) * mm, "mid": v(0, 125) * mm, "end": v(-15, 110) * mm});
            skCircle(sketch, "E84", {"center": v(0, 110) * mm, "radius": 6 * mm});
            skLineSegment(sketch, "E85", {"start": v(0, 110) * mm, "end": v(0, 80) * mm, "construction": true});
            skLineSegment(sketch, "E86", {"start": v(-90, 0) * mm, "end": v(90, 0) * mm, "construction": true});
            skLineSegment(sketch, "E87.MirrorCS", {"start": v(-33, -80) * mm, "end": v(-15, -98) * mm});
            skLineSegment(sketch, "E88.MirrorCS", {"start": v(33, -80) * mm, "end": v(15, -98) * mm});
            skLineSegment(sketch, "E89.MirrorCS", {"start": v(15, -98) * mm, "end": v(15, -110) * mm});
            skLineSegment(sketch, "E90.MirrorCS", {"start": v(-15, -98) * mm, "end": v(-15, -110) * mm});
            skArc(sketch, "E91.MirrorCS", {"start": v(15, -110) * mm, "mid": v(0, -125) * mm, "end": v(-15, -110) * mm});
            skCircle(sketch, "E92.MirrorC", {"center": v(0, -110) * mm, "radius": 6 * mm});
            skLineSegment(sketch, "E93.MirrorCS", {"start": v(0, -110) * mm, "end": v(0, -80) * mm, "construction": true});
            skSolve(sketch);
        }
        {
            var Q0;
            {var subQ1=sQuery(id+"F16.wireOp",EDGE,"E79");Q0=makeQuery(id+"F16.imprint","IMPRINT",FACE,{"disambiguationData":[TD([[makeQuery(id+"F16.imprint","IMPRINT",EDGE,{"derivedFrom":subQ1}),-1.0]])]});}
            var Q1;
            Q1=makeQuery(id+"F16.imprint","IMPRINT",FACE,{"disambiguationData":[TD([[makeQuery(id+"F16.imprint","IMPRINT",EDGE,{"derivedFrom":sQuery(id+"F16.wireOp",EDGE,"E90.MirrorCS")}),1.0]])]});
            var Q2;
            Q2=makeQuery(id+"F16.imprint","IMPRINT",FACE,{"disambiguationData":[TD([[makeQuery(id+"F16.imprint","IMPRINT",EDGE,{"derivedFrom":makeQuery(id+"F1.opExtrude","CAP_EDGE",EDGE,{"disambiguationData":[OSD([sQuery(id+"F0.wireOp",EDGE,"E1.left")])],"isStart":true})}),-1.0]])]});
            var Q3;
            Q3=makeQuery(id+"F2.opExtrude","CAP_FACE",FACE,{"disambiguationData":[OSD([sQuery(id+"F0.wireOp",EDGE,"E12"),sQuery(id+"F0.wireOp",EDGE,"E13"),sQuery(id+"F0.wireOp",EDGE,"E14"),sQuery(id+"F0.wireOp",EDGE,"E15"),sQuery(id+"F0.wireOp",EDGE,"E17.filletArc"),sQuery(id+"F0.wireOp",EDGE,"E18.filletArc"),sQuery(id+"F0.wireOp",EDGE,"E19.filletArc"),sQuery(id+"F0.wireOp",EDGE,"E20.filletArc"),sQuery(id+"F0.wireOp",EDGE,"E25.0"),sQuery(id+"F0.wireOp",EDGE,"E25.1"),sQuery(id+"F0.wireOp",EDGE,"E25.2"),sQuery(id+"F0.wireOp",EDGE,"E25.3"),sQuery(id+"F0.wireOp",EDGE,"E25.4"),sQuery(id+"F0.wireOp",EDGE,"E25.5"),sQuery(id+"F0.wireOp",EDGE,"E25.6"),sQuery(id+"F0.wireOp",EDGE,"E25.7")])],"isStart":false});
            extrude(context, id + "F17", {"entities" : qUnion([Q0, Q1, Q2]), "endBound" : BoundingType.UP_TO_SURFACE, "endBoundEntityFace" : qUnion([Q3]), "depth" : 25 * mm});
        }
    });
